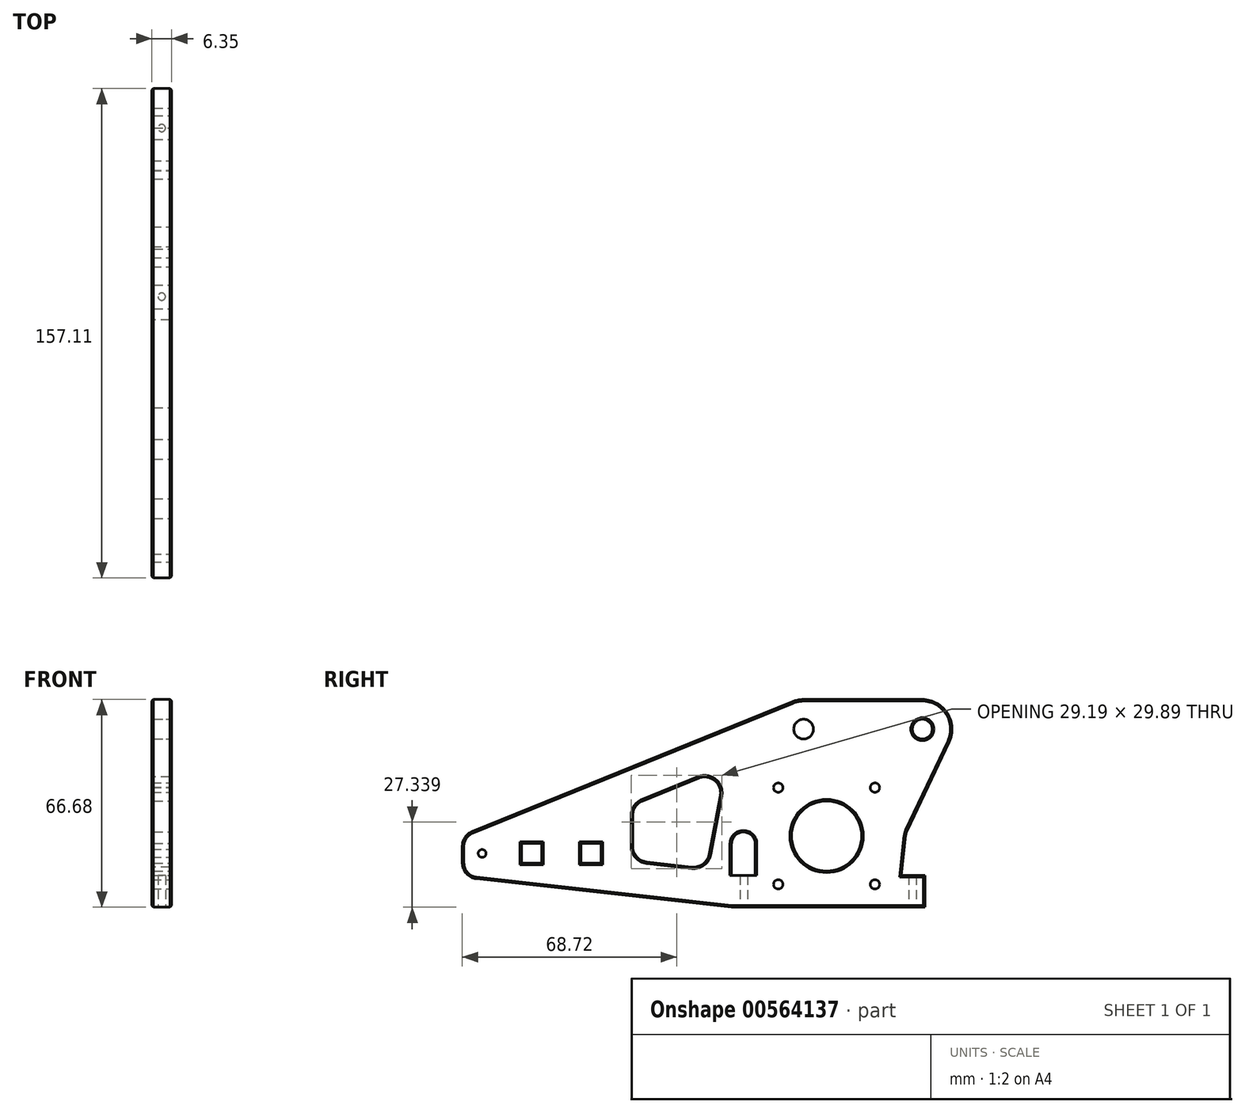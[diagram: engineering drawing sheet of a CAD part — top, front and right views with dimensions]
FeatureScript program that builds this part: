
annotation { "Feature Type Name" : "Feature", "Feature Type Description" : "" }
export const myFeature = defineFeature(function(context is Context, id is Id, definition is map)
    precondition{}
    {
        {
            var Q0;
            Q0=qCreatedBy(makeId("Right.planeOp"),FACE);
            var sketch = newSketch(context, id + "F0", { "sketchPlane" : qUnion([Q0])});
            skCircle(sketch, "E0", {"center": v(0, 0) * mm, "radius": 3.19 * mm});
            skCircle(sketch, "E1", {"center": v(-38.1, 0) * mm, "radius": 3.18 * mm});
            skCircle(sketch, "E2", {"center": v(0, 0) * mm, "radius": 9.53 * mm});
            skCircle(sketch, "E3", {"center": v(-38.1, 0) * mm, "radius": 9.53 * mm});
            skPoint(sketch, "E4", {"position": v(-30.73, -34.28) * mm});
            skLineSegment(sketch, "E5.bottom", {"start": v(-15.21, -18.76) * mm, "end": v(-46.25, -18.76) * mm});
            skLineSegment(sketch, "E5.top", {"start": v(-15.21, -49.8) * mm, "end": v(-46.25, -49.8) * mm});
            skLineSegment(sketch, "E5.left", {"start": v(-15.21, -18.76) * mm, "end": v(-15.21, -49.8) * mm});
            skLineSegment(sketch, "E5.right", {"start": v(-46.25, -18.76) * mm, "end": v(-46.25, -49.8) * mm});
            skCircle(sketch, "E6", {"center": v(-30.73, -34.28) * mm, "radius": 11.25 * mm});
            skLineSegment(sketch, "E7", {"start": v(-30.73, -34.28) * mm, "end": v(0, 0) * mm});
            skCircle(sketch, "E8", {"center": v(-15.21, -18.76) * mm, "radius": 1.5 * mm});
            skCircle(sketch, "E9", {"center": v(-46.25, -18.76) * mm, "radius": 1.5 * mm});
            skCircle(sketch, "E10", {"center": v(-46.25, -49.8) * mm, "radius": 1.5 * mm});
            skCircle(sketch, "E11", {"center": v(-15.21, -49.8) * mm, "radius": 1.5 * mm});
            skLineSegment(sketch, "E12", {"start": v(-38.1, 9.53) * mm, "end": v(0, 9.53) * mm});
            skLineSegment(sketch, "E13", {"start": v(-53.6, -57.15) * mm, "end": v(-10.42, -57.15) * mm});
            skLineSegment(sketch, "E14", {"start": v(-10.42, -57.15) * mm, "end": v(8.96, -3.22) * mm});
            skLineSegment(sketch, "E15", {"start": v(-53.6, -57.15) * mm, "end": v(-53.6, -2.03) * mm});
            skLineSegment(sketch, "E16", {"start": v(-53.6, -2.03) * mm, "end": v(-44.84, 6.74) * mm});
            skLineSegment(sketch, "E17.bottom", {"start": v(-52.33, -12.68) * mm, "end": v(-9.13, -12.68) * mm});
            skLineSegment(sketch, "E17.top", {"start": v(-52.33, -55.88) * mm, "end": v(-9.13, -55.88) * mm});
            skLineSegment(sketch, "E17.left", {"start": v(-52.33, -12.68) * mm, "end": v(-52.33, -55.88) * mm});
            skLineSegment(sketch, "E17.right", {"start": v(-9.13, -12.68) * mm, "end": v(-9.13, -55.88) * mm});
            skLineSegment(sketch, "E18.bottom", {"start": v(-53.6, -57.15) * mm, "end": v(-61.22, -57.15) * mm});
            skLineSegment(sketch, "E18.top", {"start": v(-53.6, -47) * mm, "end": v(-61.22, -47) * mm});
            skLineSegment(sketch, "E18.left", {"start": v(-53.6, -57.15) * mm, "end": v(-53.6, -47) * mm});
            skLineSegment(sketch, "E18.right", {"start": v(-61.22, -57.15) * mm, "end": v(-61.22, -47) * mm});
            skLineSegment(sketch, "E19.bottom", {"start": v(-10.42, -57.15) * mm, "end": v(0.85, -57.15) * mm});
            skLineSegment(sketch, "E19.right", {"start": v(0.85, -57.15) * mm, "end": v(0.85, -47) * mm});
            skPoint(sketch, "E20", {"position": v(-6.77, -47) * mm});
            skLineSegment(sketch, "E21.trimOffspring", {"start": v(-6.77, -47) * mm, "end": v(0.85, -47) * mm});
            skLineSegment(sketch, "E22", {"start": v(-47.55, 1.19) * mm, "end": v(-53.6, -47) * mm});
            skLineSegment(sketch, "E23.bottom", {"start": v(-61.22, -36.83) * mm, "end": v(-53.6, -36.83) * mm});
            skLineSegment(sketch, "E23.top", {"start": v(-61.22, -47) * mm, "end": v(-53.6, -47) * mm});
            skLineSegment(sketch, "E23.left", {"start": v(-61.22, -36.83) * mm, "end": v(-61.22, -47) * mm});
            skLineSegment(sketch, "E23.right", {"start": v(-53.6, -36.83) * mm, "end": v(-53.6, -47) * mm});
            skPoint(sketch, "E23.middle", {"position": v(-57.41, -41.91) * mm});
            skPoint(sketch, "E23.middle.positionSnap0", {"position": v(-57.41, -47) * mm});
            skPoint(sketch, "E23.centerSnap0", {"position": v(-57.41, -47) * mm});
            skCircle(sketch, "E24", {"center": v(-57.41, -36.83) * mm, "radius": 3.81 * mm});
            skLineSegment(sketch, "E25.bottom", {"start": v(-103.1, -36.7) * mm, "end": v(-109.48, -36.7) * mm});
            skLineSegment(sketch, "E25.top", {"start": v(-103.1, -43.07) * mm, "end": v(-109.48, -43.07) * mm});
            skLineSegment(sketch, "E25.left", {"start": v(-103.1, -36.7) * mm, "end": v(-103.1, -43.07) * mm});
            skLineSegment(sketch, "E25.right", {"start": v(-109.48, -36.7) * mm, "end": v(-109.48, -43.07) * mm});
            skPoint(sketch, "E25.middle", {"position": v(-106.3, -39.88) * mm});
            skLineSegment(sketch, "E26.bottom", {"start": v(-122.16, -36.7) * mm, "end": v(-128.53, -36.7) * mm});
            skLineSegment(sketch, "E26.top", {"start": v(-122.16, -43.07) * mm, "end": v(-128.53, -43.07) * mm});
            skLineSegment(sketch, "E26.left", {"start": v(-128.53, -36.7) * mm, "end": v(-128.53, -43.07) * mm});
            skLineSegment(sketch, "E26.right", {"start": v(-122.16, -36.7) * mm, "end": v(-122.16, -43.07) * mm});
            skPoint(sketch, "E26.middle", {"position": v(-125.35, -39.88) * mm});
            skPoint(sketch, "E26.middle.positionSnap0", {"position": v(-103.1, -39.88) * mm});
            skPoint(sketch, "E26.centerSnap0", {"position": v(-103.1, -39.88) * mm});
            skLineSegment(sketch, "E27", {"start": v(-125.35, -39.88) * mm, "end": v(-106.3, -39.88) * mm});
            skPoint(sketch, "E28", {"position": v(-115.82, -39.88) * mm});
            skLineSegment(sketch, "E29", {"start": v(-41.68, 8.83) * mm, "end": v(-147.58, -34.15) * mm});
            skLineSegment(sketch, "E30", {"start": v(-147.58, -34.15) * mm, "end": v(-147.58, -47.51) * mm});
            skLineSegment(sketch, "E31", {"start": v(-147.58, -47.51) * mm, "end": v(-61.22, -57.15) * mm});
            skLineSegment(sketch, "E32", {"start": v(-63.12, -12.21) * mm, "end": v(-92.95, -24.31) * mm});
            skLineSegment(sketch, "E33", {"start": v(-92.95, -24.31) * mm, "end": v(-92.95, -42.1) * mm});
            skLineSegment(sketch, "E34", {"start": v(-92.95, -42.1) * mm, "end": v(-69.24, -44.75) * mm});
            skLineSegment(sketch, "E35", {"start": v(-69.24, -44.75) * mm, "end": v(-63.12, -12.21) * mm});
            skLineSegment(sketch, "E36", {"start": v(-6.77, -47) * mm, "end": v(-5.25, -33.32) * mm});
            skLineSegment(sketch, "E37", {"start": v(-5.25, -33.32) * mm, "end": v(8.6, -4.08) * mm});
            skCircle(sketch, "E38", {"center": v(-141.23, -39.88) * mm, "radius": 1.27 * mm});
            skPoint(sketch, "E38.centerSnap0", {"position": v(-147.58, -39.88) * mm});
            skSolve(sketch);
        }
        {
            var Q0;
            Q0=makeQuery(id+"F0.imprint","IMPRINT",FACE,{"disambiguationData":[TD([[makeQuery(id+"F0.imprint","IMPRINT",EDGE,{"derivedFrom":sQuery(id+"F0.wireOp",EDGE,"E1")}),-1.0]])]});
            var Q1;
            Q1=makeQuery(id+"F0.imprint","IMPRINT",FACE,{"disambiguationData":[TD([[makeQuery(id+"F0.imprint","IMPRINT",EDGE,{"derivedFrom":sQuery(id+"F0.wireOp",EDGE,"E0")}),-1.0]])]});
            var Q2;
            Q2=makeQuery(id+"F0.imprint","IMPRINT",FACE,{"disambiguationData":[TD([[makeQuery(id+"F0.imprint","IMPRINT",EDGE,{"derivedFrom":sQuery(id+"F0.wireOp",EDGE,"E13")}),1.0]])]});
            var Q3;
            {var subQ0=sQuery(id+"F0.wireOp",EDGE,"E12");Q3=makeQuery(id+"F0.imprint","IMPRINT",FACE,{"disambiguationData":[TD([[makeQuery(id+"F0.imprint","IMPRINT",EDGE,{"derivedFrom":subQ0}),-1.0]])]});}
            var Q4;
            {var subQ25=sQuery(id+"F0.wireOp",EDGE,"E17.top");Q4=makeQuery(id+"F0.imprint","IMPRINT",FACE,{"disambiguationData":[TD([[makeQuery(id+"F0.imprint","IMPRINT",EDGE,{"derivedFrom":subQ25}),1.0]])]});}
            var Q5;
            Q5=makeQuery(id+"F0.imprint","IMPRINT",FACE,{"disambiguationData":[TD([[makeQuery(id+"F0.imprint","IMPRINT",EDGE,{"derivedFrom":sQuery(id+"F0.wireOp",EDGE,"E6")}),-1.0]])]});
            var Q6;
            Q6=makeQuery(id+"F0.imprint","IMPRINT",FACE,{"disambiguationData":[TD([[makeQuery(id+"F0.imprint","IMPRINT",EDGE,{"derivedFrom":sQuery(id+"F0.wireOp",EDGE,"E18.bottom")}),-1.0]])]});
            var Q7;
            {var subQ0=sQuery(id+"F0.wireOp",EDGE,"E19.bottom");Q7=makeQuery(id+"F0.imprint","IMPRINT",FACE,{"disambiguationData":[TD([[makeQuery(id+"F0.imprint","IMPRINT",EDGE,{"derivedFrom":subQ0}),1.0]])]});}
            var Q8;
            {var subQ0=sQuery(id+"F0.wireOp",EDGE,"E15");var subQ1=sQuery(id+"F0.wireOp",EDGE,"E3");var subQ2=makeQuery(id+"F0.imprint","INTERSECT",VERTEX,{"disambiguationData":[OD(0.0)],"derivedFrom":[subQ1,subQ0]});Q8=makeQuery(id+"F0.imprint","IMPRINT",FACE,{"disambiguationData":[TD([[makeQuery(id+"F0.imprint","IMPRINT",EDGE,{"disambiguationData":[TD([[subQ2,-1.0]])],"derivedFrom":subQ1}),1.0]])]});}
            var Q9;
            {var subQ0=sQuery(id+"F0.wireOp",EDGE,"E22");Q9=makeQuery(id+"F0.imprint","IMPRINT",FACE,{"disambiguationData":[TD([[makeQuery(id+"F0.imprint","IMPRINT",EDGE,{"derivedFrom":subQ0}),1.0]])]});}
            var Q10;
            {var subQ0=sQuery(id+"F0.wireOp",EDGE,"Hy1win6f-HDLC-QjAb-pHeg-SkEF8SAuvXfH");Q10=makeQuery(id+"F0.imprint","IMPRINT",FACE,{"disambiguationData":[TD([[makeQuery(id+"F0.imprint","IMPRINT",EDGE,{"derivedFrom":subQ0}),1.0]])]});}
            var Q11;
            {var subQ6=sQuery(id+"F0.wireOp",EDGE,"E16");Q11=makeQuery(id+"F0.imprint","IMPRINT",FACE,{"disambiguationData":[TD([[makeQuery(id+"F0.imprint","IMPRINT",EDGE,{"derivedFrom":subQ6}),1.0]])]});}
            var Q12;
            {var subQ0=sQuery(id+"F0.wireOp",EDGE,"E22");var subQ1=sQuery(id+"F0.wireOp",EDGE,"E3");var subQ2=makeQuery(id+"F0.imprint","INTERSECT",VERTEX,{"derivedFrom":[subQ1,subQ0]});Q12=makeQuery(id+"F0.imprint","IMPRINT",FACE,{"disambiguationData":[TD([[makeQuery(id+"F0.imprint","IMPRINT",EDGE,{"disambiguationData":[TD([[subQ2,-1.0]])],"derivedFrom":subQ1}),-1.0]])]});}
            var Q13;
            Q13=makeQuery(id+"F0.imprint","IMPRINT",FACE,{"disambiguationData":[TD([[makeQuery(id+"F0.imprint","IMPRINT",EDGE,{"derivedFrom":sQuery(id+"F0.wireOp",EDGE,"E18.right")}),1.0]])]});
            var Q14;
            Q14=makeQuery(id+"F0.imprint","IMPRINT",FACE,{"disambiguationData":[TD([[makeQuery(id+"F0.imprint","IMPRINT",EDGE,{"derivedFrom":sQuery(id+"F0.wireOp",EDGE,"E15")}),-1.0]])]});
            var Q15;
            {var subQ0=sQuery(id+"F0.wireOp",EDGE,"E17.left");var subQ1=sQuery(id+"F0.wireOp",EDGE,"E17.bottom");var subQ2=makeQuery(id+"F0.imprint","INTERSECT",VERTEX,{"derivedFrom":[subQ1,subQ0]});Q15=makeQuery(id+"F0.imprint","IMPRINT",FACE,{"disambiguationData":[TD([[makeQuery(id+"F0.imprint","IMPRINT",EDGE,{"disambiguationData":[TD([[subQ2,-1.0]])],"derivedFrom":subQ1}),-1.0]])]});}
            var Q16;
            {var subQ8=sQuery(id+"F0.wireOp",EDGE,"E36");Q16=makeQuery(id+"F0.imprint","IMPRINT",FACE,{"disambiguationData":[TD([[makeQuery(id+"F0.imprint","IMPRINT",EDGE,{"derivedFrom":subQ8}),1.0]])]});}
            var Q17;
            {var subQ6=sQuery(id+"F0.wireOp",EDGE,"E5.bottom");var subQ11=sQuery(id+"F0.wireOp",EDGE,"E7");var subQ15=makeQuery(id+"F0.imprint","INTERSECT",VERTEX,{"derivedFrom":[subQ6,subQ11]});Q17=makeQuery(id+"F0.imprint","IMPRINT",FACE,{"disambiguationData":[TD([[makeQuery(id+"F0.imprint","IMPRINT",EDGE,{"disambiguationData":[TD([[subQ15,-1.0]])],"derivedFrom":subQ6}),-1.0]])]});}
            extrude(context, id + "F1", {"entities" : qUnion([Q0, Q1, Q2, Q3, Q4, Q5, Q6, Q7, Q8, Q9, Q10, Q11, Q12, Q13, Q14, Q15, Q16, Q17]), "oppositeDirection" : true, "depth" : 6.35 * mm, "offsetDistance" : 25.4 * mm});
        }
        {
            var Q0;
            Q0=makeQuery(id+"F1.opExtrude","SWEPT_FACE",FACE,{"disambiguationData":[OSD([sQuery(id+"F0.wireOp",EDGE,"E13"),sQuery(id+"F0.wireOp",EDGE,"E18.bottom"),sQuery(id+"F0.wireOp",EDGE,"E19.bottom")])]});
            var sketch = newSketch(context, id + "F2", { "sketchPlane" : qUnion([Q0])});
            skCircle(sketch, "E39", {"center": v(-3.18, 57.28) * mm, "radius": 1.2 * mm});
            skPoint(sketch, "E39.centerSnap0", {"position": v(-3.18, 61.22) * mm});
            skCircle(sketch, "E40", {"center": v(-3.18, 3.18) * mm, "radius": 1.2 * mm});
            skPoint(sketch, "E40.centerSnap0", {"position": v(-3.18, -0.85) * mm});
            skSolve(sketch);
        }
        {
            var Q0;
            Q0 = qSketchRegion(id + "F2", true);
            extrude(context, id + "F3", {"entities" : qUnion([Q0]), "operationType" : NewBodyOperationType.REMOVE, "endBound" : BoundingType.UP_TO_NEXT, "oppositeDirection" : true, "depth" : 25.4 * mm, "offsetDistance" : 25.4 * mm});
        }
        {
            var Q0;
            Q0=makeQuery(id+"F1.opExtrude","SWEPT_EDGE",EDGE,{"disambiguationData":[OSD([sQuery(id+"F0.wireOp",EDGE,"E29"),sQuery(id+"F0.wireOp",EDGE,"E30")])]});
            var Q1;
            Q1=makeQuery(id+"F1.opExtrude","SWEPT_EDGE",EDGE,{"disambiguationData":[OSD([sQuery(id+"F0.wireOp",EDGE,"E30"),sQuery(id+"F0.wireOp",EDGE,"E31")])]});
            var Q2;
            Q2=makeQuery(id+"F1.opExtrude","SWEPT_EDGE",EDGE,{"disambiguationData":[OSD([sQuery(id+"F0.wireOp",EDGE,"E34"),sQuery(id+"F0.wireOp",EDGE,"E35")])]});
            var Q3;
            Q3=makeQuery(id+"F1.opExtrude","SWEPT_EDGE",EDGE,{"disambiguationData":[OSD([sQuery(id+"F0.wireOp",EDGE,"E33"),sQuery(id+"F0.wireOp",EDGE,"E34")])]});
            var Q4;
            Q4=makeQuery(id+"F1.opExtrude","SWEPT_EDGE",EDGE,{"disambiguationData":[OSD([sQuery(id+"F0.wireOp",EDGE,"E32"),sQuery(id+"F0.wireOp",EDGE,"E33")])]});
            var Q5;
            Q5=makeQuery(id+"F1.opExtrude","SWEPT_EDGE",EDGE,{"disambiguationData":[OSD([sQuery(id+"F0.wireOp",EDGE,"E32"),sQuery(id+"F0.wireOp",EDGE,"E35")])]});
            var Q6;
            Q6=makeQuery(id+"F1.opExtrude","SWEPT_EDGE",EDGE,{"disambiguationData":[OSD([sQuery(id+"F0.wireOp",EDGE,"E36"),sQuery(id+"F0.wireOp",EDGE,"E37")])]});
            fillet(context, id + "F4", {"entities" : qUnion([Q0, Q1, Q2, Q3, Q4, Q5, Q6]), "radius" : 5.08 * mm, "tangentPropagation" : true, "allowEdgeOverflow" : false});
        }
        {
            var Q0;
            Q0=makeQuery(id+"F1.opExtrude","CAP_EDGE",EDGE,{"disambiguationData":[OSD([sQuery(id+"F0.wireOp",EDGE,"E29")])],"isStart":true});
            var Q1;
            Q1=makeQuery(id+"F1.opExtrude","CAP_EDGE",EDGE,{"disambiguationData":[OSD([sQuery(id+"F0.wireOp",EDGE,"E13"),sQuery(id+"F0.wireOp",EDGE,"E18.bottom"),sQuery(id+"F0.wireOp",EDGE,"E19.bottom")])],"isStart":true});
            var Q2;
            Q2=makeQuery(id+"F1.opExtrude","CAP_EDGE",EDGE,{"disambiguationData":[OSD([sQuery(id+"F0.wireOp",EDGE,"E19.right")])],"isStart":true});
            var Q3;
            Q3=makeQuery(id+"F1.opExtrude","CAP_EDGE",EDGE,{"disambiguationData":[OSD([sQuery(id+"F0.wireOp",EDGE,"E19.right")])],"isStart":false});
            var Q4;
            Q4=makeQuery(id+"F1.opExtrude","CAP_EDGE",EDGE,{"disambiguationData":[OSD([sQuery(id+"F0.wireOp",EDGE,"E14")])],"isStart":false});
            var Q5;
            Q5=makeQuery(id+"F1.opExtrude","CAP_EDGE",EDGE,{"disambiguationData":[OSD([sQuery(id+"F0.wireOp",EDGE,"E13"),sQuery(id+"F0.wireOp",EDGE,"E18.bottom"),sQuery(id+"F0.wireOp",EDGE,"E19.bottom")])],"isStart":false});
            var Q6;
            Q6=makeQuery(id+"F1.opExtrude","CAP_EDGE",EDGE,{"disambiguationData":[OSD([sQuery(id+"F0.wireOp",EDGE,"E31")])],"isStart":false});
            var Q7;
            Q7=makeQuery(id+"F1.opExtrude","CAP_EDGE",EDGE,{"disambiguationData":[OSD([sQuery(id+"F0.wireOp",EDGE,"E34")])],"isStart":true});
            var Q8;
            Q8=makeQuery(id+"F1.opExtrude","CAP_EDGE",EDGE,{"disambiguationData":[OSD([sQuery(id+"F0.wireOp",EDGE,"E25.bottom")])],"isStart":false});
            var Q9;
            Q9=makeQuery(id+"F1.opExtrude","CAP_EDGE",EDGE,{"disambiguationData":[OSD([sQuery(id+"F0.wireOp",EDGE,"E25.left")])],"isStart":false});
            var Q10;
            Q10=makeQuery(id+"F1.opExtrude","CAP_EDGE",EDGE,{"disambiguationData":[OSD([sQuery(id+"F0.wireOp",EDGE,"E25.top")])],"isStart":false});
            var Q11;
            Q11=makeQuery(id+"F1.opExtrude","CAP_EDGE",EDGE,{"disambiguationData":[OSD([sQuery(id+"F0.wireOp",EDGE,"E25.right")])],"isStart":false});
            var Q12;
            Q12=makeQuery(id+"F1.opExtrude","CAP_EDGE",EDGE,{"disambiguationData":[OSD([sQuery(id+"F0.wireOp",EDGE,"E26.right")])],"isStart":false});
            var Q13;
            Q13=makeQuery(id+"F1.opExtrude","CAP_EDGE",EDGE,{"disambiguationData":[OSD([sQuery(id+"F0.wireOp",EDGE,"E26.top")])],"isStart":false});
            var Q14;
            Q14=makeQuery(id+"F1.opExtrude","CAP_EDGE",EDGE,{"disambiguationData":[OSD([sQuery(id+"F0.wireOp",EDGE,"E26.left")])],"isStart":false});
            var Q15;
            Q15=makeQuery(id+"F1.opExtrude","CAP_EDGE",EDGE,{"disambiguationData":[OSD([sQuery(id+"F0.wireOp",EDGE,"E26.bottom")])],"isStart":false});
            var Q16;
            Q16=makeQuery(id+"F1.opExtrude","CAP_EDGE",EDGE,{"disambiguationData":[OSD([sQuery(id+"F0.wireOp",EDGE,"E26.bottom")])],"isStart":true});
            var Q17;
            Q17=makeQuery(id+"F1.opExtrude","CAP_EDGE",EDGE,{"disambiguationData":[OSD([sQuery(id+"F0.wireOp",EDGE,"E26.left")])],"isStart":true});
            var Q18;
            Q18=makeQuery(id+"F1.opExtrude","CAP_EDGE",EDGE,{"disambiguationData":[OSD([sQuery(id+"F0.wireOp",EDGE,"E26.top")])],"isStart":true});
            var Q19;
            Q19=makeQuery(id+"F1.opExtrude","CAP_EDGE",EDGE,{"disambiguationData":[OSD([sQuery(id+"F0.wireOp",EDGE,"E26.right")])],"isStart":true});
            var Q20;
            Q20=makeQuery(id+"F1.opExtrude","CAP_EDGE",EDGE,{"disambiguationData":[OSD([sQuery(id+"F0.wireOp",EDGE,"E25.top")])],"isStart":true});
            var Q21;
            Q21=makeQuery(id+"F1.opExtrude","CAP_EDGE",EDGE,{"disambiguationData":[OSD([sQuery(id+"F0.wireOp",EDGE,"E25.right")])],"isStart":true});
            var Q22;
            Q22=makeQuery(id+"F1.opExtrude","CAP_EDGE",EDGE,{"disambiguationData":[OSD([sQuery(id+"F0.wireOp",EDGE,"E25.bottom")])],"isStart":true});
            var Q23;
            Q23=makeQuery(id+"F1.opExtrude","CAP_EDGE",EDGE,{"disambiguationData":[OSD([sQuery(id+"F0.wireOp",EDGE,"E25.left")])],"isStart":true});
            var Q24;
            Q24=makeQuery(id+"F1.opExtrude","CAP_EDGE",EDGE,{"disambiguationData":[OSD([sQuery(id+"F0.wireOp",EDGE,"E23.left")])],"isStart":true});
            var Q25;
            Q25=makeQuery(id+"F1.opExtrude","CAP_EDGE",EDGE,{"disambiguationData":[OSD([sQuery(id+"F0.wireOp",EDGE,"E23.left")])],"isStart":false});
            var Q26;
            Q26=makeQuery(id+"F1.opExtrude","SWEPT_FACE",FACE,{"disambiguationData":[OSD([sQuery(id+"F0.wireOp",EDGE,"E6")])]});
            var Q27;
            Q27=makeQuery(id+"F1.opExtrude","CAP_EDGE",EDGE,{"disambiguationData":[OSD([sQuery(id+"F0.wireOp",EDGE,"E21.trimOffspring")])],"isStart":false});
            var Q28;
            Q28=makeQuery(id+"F1.opExtrude","CAP_EDGE",EDGE,{"disambiguationData":[OSD([sQuery(id+"F0.wireOp",EDGE,"E21.trimOffspring")])],"isStart":true});
            var Q29;
            Q29=makeQuery(id+"F1.opExtrude","CAP_EDGE",EDGE,{"disambiguationData":[OSD([sQuery(id+"F0.wireOp",EDGE,"E22")])],"isStart":true});
            var Q30;
            Q30=makeQuery(id+"F1.opExtrude","CAP_EDGE",EDGE,{"disambiguationData":[OSD([sQuery(id+"F0.wireOp",EDGE,"E22")])],"isStart":false});
            var Q31;
            Q31=makeQuery(id+"F1.opExtrude","CAP_EDGE",EDGE,{"disambiguationData":[OSD([sQuery(id+"F0.wireOp",EDGE,"E34")])],"isStart":false});
            var Q32;
            Q32=makeQuery(id+"F1.opExtrude","SWEPT_FACE",FACE,{"disambiguationData":[OSD([sQuery(id+"F0.wireOp",EDGE,"E0")])]});
            chamfer(context, id + "F5", {"entities" : qUnion([Q0, Q1, Q2, Q3, Q4, Q5, Q6, Q7, Q8, Q9, Q10, Q11, Q12, Q13, Q14, Q15, Q16, Q17, Q18, Q19, Q20, Q21, Q22, Q23, Q24, Q25, Q26, Q27, Q28, Q29, Q30, Q31, Q32]), "width" : 0.5 * mm, "tangentPropagation" : true});
        }
    });
